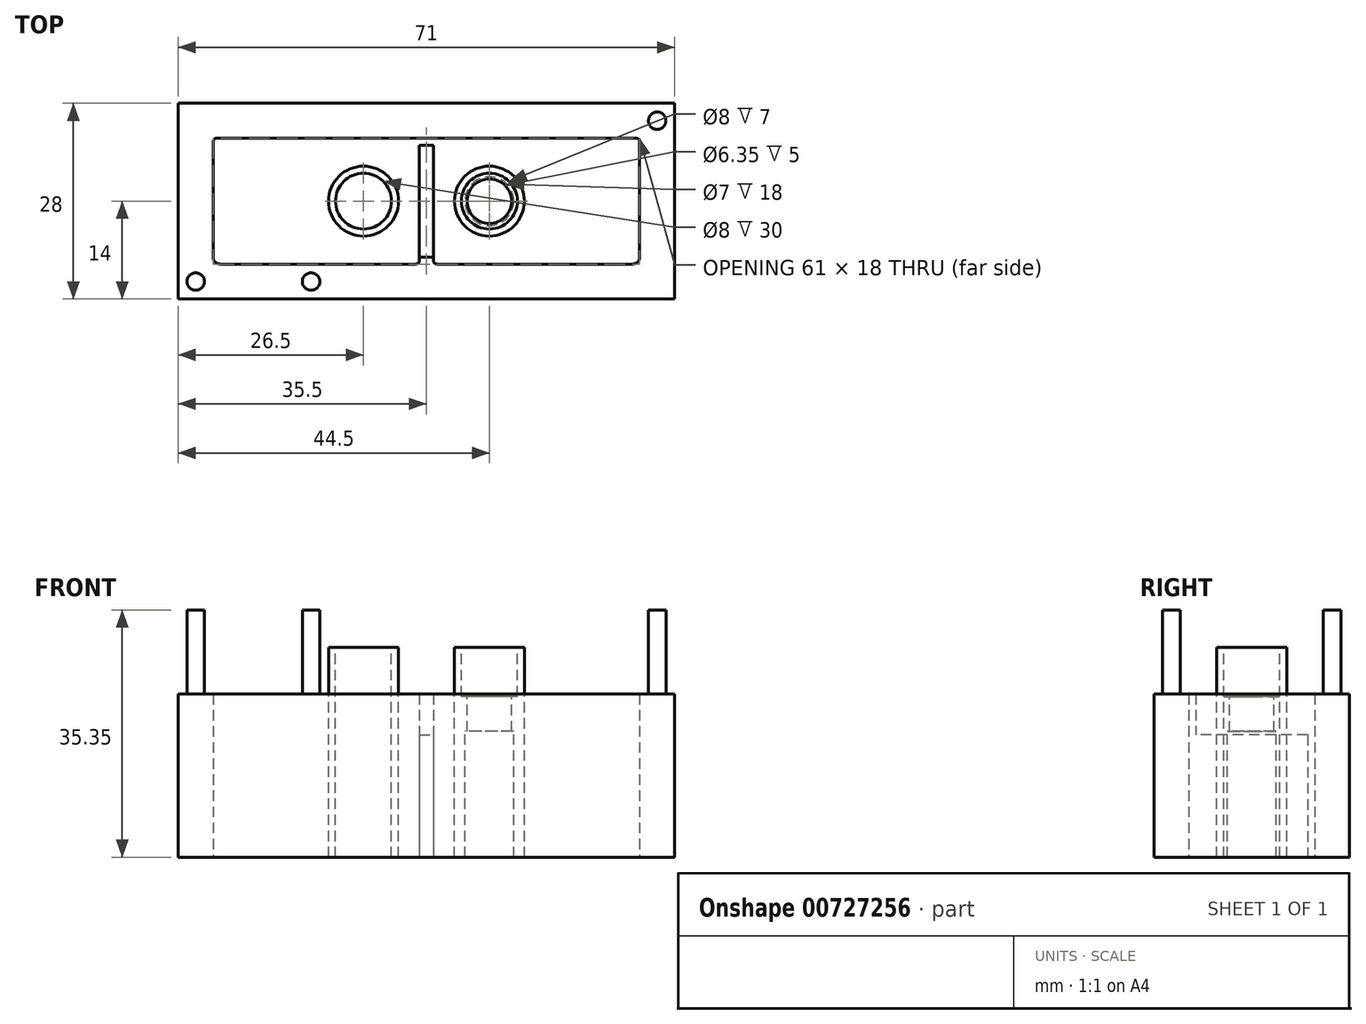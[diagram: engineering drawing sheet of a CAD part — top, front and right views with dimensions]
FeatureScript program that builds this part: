
annotation { "Feature Type Name" : "Feature", "Feature Type Description" : "" }
export const myFeature = defineFeature(function(context is Context, id is Id, definition is map)
    precondition{}
    {
        {
            var Q0;
            Q0=qCreatedBy(makeId("Top.planeOp"),FACE);
            var sketch = newSketch(context, id + "F0", { "sketchPlane" : qUnion([Q0])});
            skLineSegment(sketch, "E0.bottom", {"start": v(-35.5, -14) * mm, "end": v(35.5, -14) * mm});
            skLineSegment(sketch, "E0.top", {"start": v(-35.5, 14) * mm, "end": v(35.5, 14) * mm});
            skLineSegment(sketch, "E0.left", {"start": v(-35.5, -14) * mm, "end": v(-35.5, 14) * mm});
            skLineSegment(sketch, "E0.right", {"start": v(35.5, -14) * mm, "end": v(35.5, 14) * mm});
            skPoint(sketch, "E0.middle", {"position": v(0, 0) * mm});
            skLineSegment(sketch, "E1.bottom", {"start": v(-30.5, -9) * mm, "end": v(30.5, -9) * mm});
            skLineSegment(sketch, "E1.top", {"start": v(-30.5, 9) * mm, "end": v(30.5, 9) * mm});
            skLineSegment(sketch, "E1.left", {"start": v(-30.5, -9) * mm, "end": v(-30.5, 9) * mm});
            skLineSegment(sketch, "E1.right", {"start": v(30.5, -9) * mm, "end": v(30.5, 9) * mm});
            skCircle(sketch, "E2", {"center": v(-9, 0) * mm, "radius": 5 * mm});
            skCircle(sketch, "E3", {"center": v(-20.4, 0) * mm, "radius": 5 * mm});
            skCircle(sketch, "E4", {"center": v(9, 0) * mm, "radius": 5 * mm});
            skCircle(sketch, "E5", {"center": v(20.4, 0) * mm, "radius": 5 * mm});
            skLineSegment(sketch, "E6.bottom", {"start": v(-1, 9) * mm, "end": v(1, 9) * mm});
            skLineSegment(sketch, "E6.top", {"start": v(-1, 8) * mm, "end": v(1, 8) * mm});
            skLineSegment(sketch, "E6.left", {"start": v(-1, 9) * mm, "end": v(-1, 8) * mm});
            skLineSegment(sketch, "E6.right", {"start": v(1, 9) * mm, "end": v(1, 8) * mm});
            skLineSegment(sketch, "E7.MirrorCS", {"start": v(-1, -8) * mm, "end": v(1, -8) * mm});
            skLineSegment(sketch, "E8.MirrorCS", {"start": v(-1, -9) * mm, "end": v(1, -9) * mm});
            skLineSegment(sketch, "E9.MirrorCS", {"start": v(1, -9) * mm, "end": v(1, -8) * mm});
            skLineSegment(sketch, "E10.MirrorCS", {"start": v(-1, -9) * mm, "end": v(-1, -8) * mm});
            skLineSegment(sketch, "E11.left", {"start": v(-1, 8) * mm, "end": v(-1, -8) * mm});
            skLineSegment(sketch, "E11.right", {"start": v(1, 8) * mm, "end": v(1, -8) * mm});
            skSolve(sketch);
        }
        {
            var Q0;
            Q0=makeQuery(id+"F0.imprint","IMPRINT",FACE,{"disambiguationData":[TD([[makeQuery(id+"F0.imprint","IMPRINT",EDGE,{"derivedFrom":sQuery(id+"F0.wireOp",EDGE,"E0.bottom")}),1.0]])]});
            var Q1;
            Q1 = qSketchRegion(id + "F0", true);
            var Q2;
            Q2=makeQuery(id+"F0.imprint","IMPRINT",FACE,{"disambiguationData":[TD([[makeQuery(id+"F0.imprint","IMPRINT",EDGE,{"derivedFrom":sQuery(id+"F0.wireOp",EDGE,"E1.bottom")}),1.0]])]});
            var Q3;
            Q3=makeQuery(id+"F0.imprint","IMPRINT",FACE,{"disambiguationData":[TD([[makeQuery(id+"F0.imprint","IMPRINT",EDGE,{"derivedFrom":sQuery(id+"F0.wireOp",EDGE,"E3")}),1.0]])]});
            var Q4;
            Q4=makeQuery(id+"F0.imprint","IMPRINT",FACE,{"disambiguationData":[TD([[makeQuery(id+"F0.imprint","IMPRINT",EDGE,{"derivedFrom":sQuery(id+"F0.wireOp",EDGE,"E2")}),1.0]])]});
            var Q5;
            Q5=makeQuery(id+"F0.imprint","IMPRINT",FACE,{"disambiguationData":[TD([[makeQuery(id+"F0.imprint","IMPRINT",EDGE,{"derivedFrom":sQuery(id+"F0.wireOp",EDGE,"E4")}),1.0]])]});
            var Q6;
            Q6=makeQuery(id+"F0.imprint","IMPRINT",FACE,{"disambiguationData":[TD([[makeQuery(id+"F0.imprint","IMPRINT",EDGE,{"derivedFrom":sQuery(id+"F0.wireOp",EDGE,"E5")}),1.0]])]});
            var Q7;
            Q7=makeQuery(id+"F0.imprint","IMPRINT",FACE,{"disambiguationData":[TD([[makeQuery(id+"F0.imprint","IMPRINT",EDGE,{"derivedFrom":sQuery(id+"F0.wireOp",EDGE,"E6.bottom")}),-1.0]])]});
            var Q8;
            Q8=makeQuery(id+"F0.imprint","IMPRINT",FACE,{"disambiguationData":[TD([[makeQuery(id+"F0.imprint","IMPRINT",EDGE,{"derivedFrom":sQuery(id+"F0.wireOp",EDGE,"E7.MirrorCS")}),-1.0]])]});
            var Q9;
            Q9=makeQuery(id+"F0.imprint","IMPRINT",FACE,{"disambiguationData":[TD([[makeQuery(id+"F0.imprint","IMPRINT",EDGE,{"derivedFrom":sQuery(id+"F0.wireOp",EDGE,"E6.top")}),-1.0]])]});
            var Q10;
            Q10=makeQuery(id+"F0.imprint","IMPRINT",FACE,{"disambiguationData":[TD([[makeQuery(id+"F0.imprint","IMPRINT",EDGE,{"derivedFrom":sQuery(id+"F0.wireOp",EDGE,"E8.MirrorCS")}),1.0]])]});
            extrude(context, id + "F1", {"entities" : qUnion([Q0, Q1, Q2, Q3, Q4, Q5, Q6, Q7, Q8, Q9, Q10]), "depth" : 5 * mm, "offsetDistance" : 25 * mm});
        }
        {
            var Q0;
            Q0=makeQuery(id+"F0.imprint","IMPRINT",FACE,{"disambiguationData":[TD([[makeQuery(id+"F0.imprint","IMPRINT",EDGE,{"derivedFrom":sQuery(id+"F0.wireOp",EDGE,"E0.bottom")}),1.0]])]});
            var Q1;
            Q1=makeQuery(id+"F0.imprint","IMPRINT",FACE,{"disambiguationData":[TD([[makeQuery(id+"F0.imprint","IMPRINT",EDGE,{"derivedFrom":sQuery(id+"F0.wireOp",EDGE,"E6.bottom")}),-1.0]])]});
            var Q2;
            Q2=makeQuery(id+"F0.imprint","IMPRINT",FACE,{"disambiguationData":[TD([[makeQuery(id+"F0.imprint","IMPRINT",EDGE,{"derivedFrom":sQuery(id+"F0.wireOp",EDGE,"E7.MirrorCS")}),-1.0]])]});
            var Q3;
            Q3=makeQuery(id+"F0.imprint","IMPRINT",FACE,{"disambiguationData":[TD([[makeQuery(id+"F0.imprint","IMPRINT",EDGE,{"derivedFrom":sQuery(id+"F0.wireOp",EDGE,"E8.MirrorCS")}),1.0]])]});
            extrude(context, id + "F2", {"entities" : qUnion([Q0, Q1, Q2, Q3]), "operationType" : NewBodyOperationType.ADD, "depth" : (5 + 25 - 1 + 6.35) * mm, "offsetDistance" : 25 * mm});
        }
        {
            var Q0;
            Q0=makeQuery(id+"F0.imprint","IMPRINT",FACE,{"disambiguationData":[TD([[makeQuery(id+"F0.imprint","IMPRINT",EDGE,{"derivedFrom":sQuery(id+"F0.wireOp",EDGE,"E6.top")}),-1.0]])]});
            extrude(context, id + "F3", {"entities" : qUnion([Q0]), "operationType" : NewBodyOperationType.ADD, "depth" : (5 + 12.5) * mm, "offsetDistance" : 25 * mm});
        }
        {
            var Q0;
            Q0=makeQuery(id+"F2.opExtrude","SWEPT_EDGE",EDGE,{"disambiguationData":[OSD([sQuery(id+"F0.wireOp",EDGE,"E1.top"),sQuery(id+"F0.wireOp",EDGE,"E6.bottom"),sQuery(id+"F0.wireOp",EDGE,"E6.left")])]});
            var Q1;
            Q1=makeQuery(id+"F2.opExtrude","SWEPT_EDGE",EDGE,{"disambiguationData":[OSD([sQuery(id+"F0.wireOp",EDGE,"E1.top"),sQuery(id+"F0.wireOp",EDGE,"E6.bottom"),sQuery(id+"F0.wireOp",EDGE,"E6.right")])]});
            var Q2;
            Q2=makeQuery(id+"F2.opExtrude","SWEPT_EDGE",EDGE,{"disambiguationData":[OSD([sQuery(id+"F0.wireOp",EDGE,"E1.bottom"),sQuery(id+"F0.wireOp",EDGE,"E8.MirrorCS"),sQuery(id+"F0.wireOp",EDGE,"E10.MirrorCS")])]});
            var Q3;
            Q3=makeQuery(id+"F2.opExtrude","SWEPT_EDGE",EDGE,{"disambiguationData":[OSD([sQuery(id+"F0.wireOp",EDGE,"E1.bottom"),sQuery(id+"F0.wireOp",EDGE,"E8.MirrorCS"),sQuery(id+"F0.wireOp",EDGE,"E9.MirrorCS")])]});
            fillet(context, id + "F4", {"entities" : qUnion([Q0, Q1, Q2, Q3]), "tangentPropagation" : true, "radius" : 0.5 * mm, "defaultsChanged" : true, "vertexSettings" : [], "allowEdgeOverflow" : false});
        }
        {
            var Q0;
            Q0=makeQuery(id+"F0.imprint","IMPRINT",FACE,{"disambiguationData":[TD([[makeQuery(id+"F0.imprint","IMPRINT",EDGE,{"derivedFrom":sQuery(id+"F0.wireOp",EDGE,"E3")}),1.0]])]});
            var Q1;
            Q1=makeQuery(id+"F0.imprint","IMPRINT",FACE,{"disambiguationData":[TD([[makeQuery(id+"F0.imprint","IMPRINT",EDGE,{"derivedFrom":sQuery(id+"F0.wireOp",EDGE,"E5")}),1.0]])]});
            var Q2;
            Q2=makeQuery(id+"F0.imprint","IMPRINT",FACE,{"disambiguationData":[TD([[makeQuery(id+"F0.imprint","IMPRINT",EDGE,{"derivedFrom":sQuery(id+"F0.wireOp",EDGE,"E2")}),1.0]])]});
            var Q3;
            Q3=makeQuery(id+"F0.imprint","IMPRINT",FACE,{"disambiguationData":[TD([[makeQuery(id+"F0.imprint","IMPRINT",EDGE,{"derivedFrom":sQuery(id+"F0.wireOp",EDGE,"E4")}),1.0]])]});
            extrude(context, id + "F5", {"entities" : qUnion([Q0, Q1, Q2, Q3]), "operationType" : NewBodyOperationType.REMOVE, "depth" : 5 * mm, "offsetDistance" : 25 * mm});
        }
        {
            var Q0;
            Q0=qCreatedBy(makeId("Front.planeOp"),FACE);
            var sketch = newSketch(context, id + "F6", { "sketchPlane" : qUnion([Q0])});
            skLineSegment(sketch, "E12.bottom", {"start": v(-14, 0) * mm, "end": v(-13, 0) * mm});
            skLineSegment(sketch, "E12.top", {"start": v(-14, 30) * mm, "end": v(-13, 30) * mm});
            skLineSegment(sketch, "E12.left", {"start": v(-14, 0) * mm, "end": v(-14, 30) * mm});
            skLineSegment(sketch, "E12.right", {"start": v(-13, 0) * mm, "end": v(-13, 30) * mm});
            skLineSegment(sketch, "E13.bottom", {"start": v(-13, 18) * mm, "end": v(-9, 18) * mm});
            skLineSegment(sketch, "E13.top", {"start": v(-13, 23) * mm, "end": v(-9, 23) * mm});
            skLineSegment(sketch, "E13.left", {"start": v(-13, 23) * mm, "end": v(-13, 18) * mm});
            skLineSegment(sketch, "E13.right", {"start": v(-9, 23) * mm, "end": v(-9, 18) * mm});
            skLineSegment(sketch, "E14.bottom", {"start": v(-13, 23) * mm, "end": v(-12.18, 23) * mm});
            skLineSegment(sketch, "E14.top", {"start": v(-13, 18) * mm, "end": v(-12.18, 18) * mm});
            skLineSegment(sketch, "E14.right", {"start": v(-12.18, 23) * mm, "end": v(-12.18, 18) * mm});
            skLineSegment(sketch, "E15.bottom", {"start": v(-13, 18) * mm, "end": v(-12.5, 18) * mm});
            skLineSegment(sketch, "E15.top", {"start": v(-13, 0) * mm, "end": v(-12.5, 0) * mm});
            skLineSegment(sketch, "E15.left", {"start": v(-13, 18) * mm, "end": v(-13, 0) * mm});
            skLineSegment(sketch, "E15.right", {"start": v(-12.5, 18) * mm, "end": v(-12.5, 0) * mm});
            skLineSegment(sketch, "E16.MirrorCS", {"start": v(13, 18) * mm, "end": v(12.5, 18) * mm});
            skLineSegment(sketch, "E17.MirrorCS", {"start": v(13, 0) * mm, "end": v(12.5, 0) * mm});
            skLineSegment(sketch, "E18.MirrorCS", {"start": v(13, 18) * mm, "end": v(12.18, 18) * mm});
            skLineSegment(sketch, "E19.MirrorCS", {"start": v(13, 23) * mm, "end": v(12.18, 23) * mm});
            skLineSegment(sketch, "E20.MirrorCS", {"start": v(14, 30) * mm, "end": v(13, 30) * mm});
            skLineSegment(sketch, "E21.MirrorCS", {"start": v(14, 0) * mm, "end": v(13, 0) * mm});
            skLineSegment(sketch, "E22.MirrorCS", {"start": v(13, 23) * mm, "end": v(13, 18) * mm});
            skLineSegment(sketch, "E23.MirrorCS", {"start": v(13, 18) * mm, "end": v(13, 0) * mm});
            skLineSegment(sketch, "E24.MirrorCS", {"start": v(14, 0) * mm, "end": v(14, 30) * mm});
            skLineSegment(sketch, "E25.MirrorCS", {"start": v(13, 0) * mm, "end": v(13, 30) * mm});
            skLineSegment(sketch, "E26.MirrorCS", {"start": v(12.18, 23) * mm, "end": v(12.18, 18) * mm});
            skLineSegment(sketch, "E27.MirrorCS", {"start": v(13, 18) * mm, "end": v(9, 18) * mm});
            skLineSegment(sketch, "E28.MirrorCS", {"start": v(12.5, 18) * mm, "end": v(12.5, 0) * mm});
            skLineSegment(sketch, "E29.MirrorCS", {"start": v(13, 23) * mm, "end": v(9, 23) * mm});
            skLineSegment(sketch, "E30.MirrorCS", {"start": v(9, 23) * mm, "end": v(9, 18) * mm});
            skSolve(sketch);
        }
        {
            var Q0;
            Q0=makeQuery(id+"F6.imprint","IMPRINT",FACE,{"disambiguationData":[TD([[makeQuery(id+"F6.imprint","IMPRINT",EDGE,{"derivedFrom":sQuery(id+"F6.wireOp",EDGE,"E12.bottom")}),1.0]])]});
            var Q1;
            Q1=makeQuery(id+"F6.imprint","IMPRINT",FACE,{"disambiguationData":[TD([[makeQuery(id+"F6.imprint","IMPRINT",EDGE,{"derivedFrom":sQuery(id+"F6.wireOp",EDGE,"E14.bottom")}),-1.0]])]});
            var Q2;
            Q2=makeQuery(id+"F6.imprint","IMPRINT",FACE,{"disambiguationData":[TD([[makeQuery(id+"F6.imprint","IMPRINT",EDGE,{"derivedFrom":sQuery(id+"F6.wireOp",EDGE,"E15.bottom")}),-1.0]])]});
            var Q3;
            Q3=sQuery(id+"F6.wireOp",EDGE,"E13.right");
            revolve(context, id + "F7", {"operationType" : NewBodyOperationType.ADD, "surfaceOperationType" : NewSurfaceOperationType.NEW, "entities" : qUnion([Q0, Q1, Q2]), "axis" : qUnion([Q3]), "revolveType" : RevolveType.FULL});
        }
        {
            var Q0;
            {var subQ2=sQuery(id+"F6.wireOp",EDGE,"E26.MirrorCS");Q0=makeQuery(id+"F6.imprint","IMPRINT",FACE,{"disambiguationData":[TD([[makeQuery(id+"F6.imprint","IMPRINT",EDGE,{"derivedFrom":subQ2}),1.0]])]});}
            var Q1;
            {var subQ3=sQuery(id+"F6.wireOp",EDGE,"E20.MirrorCS");Q1=makeQuery(id+"F6.imprint","IMPRINT",FACE,{"disambiguationData":[TD([[makeQuery(id+"F6.imprint","IMPRINT",EDGE,{"derivedFrom":subQ3}),1.0]])]});}
            var Q2;
            {var subQ0=sQuery(id+"F6.wireOp",EDGE,"E17.MirrorCS");Q2=makeQuery(id+"F6.imprint","IMPRINT",FACE,{"disambiguationData":[TD([[makeQuery(id+"F6.imprint","IMPRINT",EDGE,{"derivedFrom":subQ0}),-1.0]])]});}
            var Q3;
            Q3=sQuery(id+"F6.wireOp",EDGE,"E30.MirrorCS");
            revolve(context, id + "F8", {"operationType" : NewBodyOperationType.ADD, "surfaceOperationType" : NewSurfaceOperationType.NEW, "entities" : qUnion([Q0, Q1, Q2]), "axis" : qUnion([Q3]), "revolveType" : RevolveType.FULL});
        }
        {
            var Q0;
            {var subQ0=sQuery(id+"F0.wireOp",EDGE,"E0.left");Q0=makeQuery(id+"F2.boolean.opBoolean","MERGE",FACE,{"derivedFrom":[makeQuery(id+"F1.opExtrude","SWEPT_FACE",FACE,{"disambiguationData":[OSD([subQ0])]}),makeQuery(id+"F2.opExtrude","SWEPT_FACE",FACE,{"disambiguationData":[OSD([subQ0])]})]});}
            var sketch = newSketch(context, id + "F9", { "sketchPlane" : qUnion([Q0])});
            skCircle(sketch, "E31", {"center": v(0, 29) * mm, "radius": 3.25 * mm});
            skCircle(sketch, "E32", {"center": v(-4.3, 33.3) * mm, "radius": 1.25 * mm});
            skLineSegment(sketch, "E33", {"start": v(-13.65, 29) * mm, "end": v(14.35, 29) * mm});
            skLineSegment(sketch, "E34", {"start": v(0, 35.35) * mm, "end": v(0, 21.85) * mm});
            skCircle(sketch, "E35.MirrorC", {"center": v(-4.3, 24.7) * mm, "radius": 1.25 * mm});
            skCircle(sketch, "E36.MirrorC", {"center": v(4.3, 33.3) * mm, "radius": 1.25 * mm});
            skCircle(sketch, "E37.MirrorC", {"center": v(4.3, 24.7) * mm, "radius": 1.25 * mm});
            skSolve(sketch);
        }
        {
            var Q0;
            Q0=makeQuery(id+"F2.opExtrude","CAP_FACE",FACE,{"disambiguationData":[OSD([sQuery(id+"F0.wireOp",EDGE,"E0.bottom"),sQuery(id+"F0.wireOp",EDGE,"E0.top"),sQuery(id+"F0.wireOp",EDGE,"E0.left"),sQuery(id+"F0.wireOp",EDGE,"E0.right"),sQuery(id+"F0.wireOp",EDGE,"E1.bottom"),sQuery(id+"F0.wireOp",EDGE,"E1.top"),sQuery(id+"F0.wireOp",EDGE,"E1.left"),sQuery(id+"F0.wireOp",EDGE,"E1.right")])],"isStart":false});
            var sketch = newSketch(context, id + "F10", { "sketchPlane" : qUnion([Q0])});
            skLineSegment(sketch, "E38.bottom", {"start": v(-35.5, 14) * mm, "end": v(35.5, 14) * mm});
            skLineSegment(sketch, "E38.top", {"start": v(-35.5, -14) * mm, "end": v(35.5, -14) * mm});
            skLineSegment(sketch, "E38.left", {"start": v(-35.5, 14) * mm, "end": v(-35.5, -14) * mm});
            skLineSegment(sketch, "E38.right", {"start": v(35.5, 14) * mm, "end": v(35.5, -14) * mm});
            skCircle(sketch, "E39", {"center": v(-33, 11.5) * mm, "radius": 1.25 * mm});
            skCircle(sketch, "E40.MirrorC", {"center": v(33, 11.5) * mm, "radius": 1.25 * mm});
            skCircle(sketch, "E41.MirrorC", {"center": v(-33, -11.5) * mm, "radius": 1.25 * mm});
            skCircle(sketch, "E42.MirrorC", {"center": v(33, -11.5) * mm, "radius": 1.25 * mm});
            skCircle(sketch, "E43", {"center": v(0, 11.5) * mm, "radius": 1.25 * mm});
            skPoint(sketch, "E43.centerSnap0", {"position": v(0, 14) * mm});
            skCircle(sketch, "E44", {"center": v(-16.5, 11.5) * mm, "radius": 1.25 * mm});
            skLineSegment(sketch, "E45", {"start": v(-33, 11.5) * mm, "end": v(33, 11.5) * mm});
            skLineSegment(sketch, "E46", {"start": v(-33, 11.5) * mm, "end": v(-33, -11.5) * mm});
            skLineSegment(sketch, "E47", {"start": v(-33, -11.5) * mm, "end": v(33, -11.5) * mm});
            skLineSegment(sketch, "E48", {"start": v(33, -11.5) * mm, "end": v(33, 11.5) * mm});
            skCircle(sketch, "E49.MirrorC", {"center": v(16.5, 11.5) * mm, "radius": 1.25 * mm});
            skCircle(sketch, "E50.MirrorC", {"center": v(-16.5, -11.5) * mm, "radius": 1.25 * mm});
            skCircle(sketch, "E51.MirrorC", {"center": v(0, -11.5) * mm, "radius": 1.25 * mm});
            skCircle(sketch, "E52.MirrorC", {"center": v(16.5, -11.5) * mm, "radius": 1.25 * mm});
            skSolve(sketch);
        }
        {
            var Q0;
            {var subQ0=sQuery(id+"F10.wireOp",EDGE,"E45");var subQ1=sQuery(id+"F10.wireOp",EDGE,"E39");var subQ2=makeQuery(id+"F10.imprint","INTERSECT",VERTEX,{"derivedFrom":[subQ1,subQ0]});Q0=makeQuery(id+"F10.imprint","IMPRINT",FACE,{"disambiguationData":[TD([[makeQuery(id+"F10.imprint","IMPRINT",EDGE,{"disambiguationData":[TD([[subQ2,1.0]])],"derivedFrom":subQ1}),1.0]])]});}
            var Q1;
            {var subQ0=sQuery(id+"F10.wireOp",EDGE,"E45");var subQ1=sQuery(id+"F10.wireOp",EDGE,"E39");var subQ2=makeQuery(id+"F10.imprint","INTERSECT",VERTEX,{"derivedFrom":[subQ1,subQ0]});Q1=makeQuery(id+"F10.imprint","IMPRINT",FACE,{"disambiguationData":[TD([[makeQuery(id+"F10.imprint","IMPRINT",EDGE,{"disambiguationData":[TD([[subQ2,-1.0]])],"derivedFrom":subQ1}),1.0]])]});}
            var Q2;
            {var subQ0=sQuery(id+"F10.wireOp",EDGE,"E45");var subQ1=sQuery(id+"F10.wireOp",EDGE,"E44");var subQ2=makeQuery(id+"F10.imprint","INTERSECT",VERTEX,{"disambiguationData":[OD(0.0)],"derivedFrom":[subQ1,subQ0]});Q2=makeQuery(id+"F10.imprint","IMPRINT",FACE,{"disambiguationData":[TD([[makeQuery(id+"F10.imprint","IMPRINT",EDGE,{"disambiguationData":[TD([[subQ2,-1.0]])],"derivedFrom":subQ1}),1.0]])]});}
            var Q3;
            {var subQ0=sQuery(id+"F10.wireOp",EDGE,"E45");var subQ1=sQuery(id+"F10.wireOp",EDGE,"E44");var subQ2=makeQuery(id+"F10.imprint","INTERSECT",VERTEX,{"disambiguationData":[OD(0.0)],"derivedFrom":[subQ1,subQ0]});Q3=makeQuery(id+"F10.imprint","IMPRINT",FACE,{"disambiguationData":[TD([[makeQuery(id+"F10.imprint","IMPRINT",EDGE,{"disambiguationData":[TD([[subQ2,1.0]])],"derivedFrom":subQ1}),1.0]])]});}
            var Q4;
            {var subQ0=sQuery(id+"F10.wireOp",EDGE,"E45");var subQ1=sQuery(id+"F10.wireOp",EDGE,"E43");var subQ2=makeQuery(id+"F10.imprint","INTERSECT",VERTEX,{"disambiguationData":[OD(0.0)],"derivedFrom":[subQ1,subQ0]});Q4=makeQuery(id+"F10.imprint","IMPRINT",FACE,{"disambiguationData":[TD([[makeQuery(id+"F10.imprint","IMPRINT",EDGE,{"disambiguationData":[TD([[subQ2,-1.0]])],"derivedFrom":subQ1}),1.0]])]});}
            var Q5;
            {var subQ0=sQuery(id+"F10.wireOp",EDGE,"E45");var subQ1=sQuery(id+"F10.wireOp",EDGE,"E43");var subQ2=makeQuery(id+"F10.imprint","INTERSECT",VERTEX,{"disambiguationData":[OD(0.0)],"derivedFrom":[subQ1,subQ0]});Q5=makeQuery(id+"F10.imprint","IMPRINT",FACE,{"disambiguationData":[TD([[makeQuery(id+"F10.imprint","IMPRINT",EDGE,{"disambiguationData":[TD([[subQ2,1.0]])],"derivedFrom":subQ1}),1.0]])]});}
            var Q6;
            {var subQ0=sQuery(id+"F10.wireOp",EDGE,"E49.MirrorC");var subQ1=sQuery(id+"F10.wireOp",EDGE,"E45");var subQ2=makeQuery(id+"F10.imprint","INTERSECT",VERTEX,{"disambiguationData":[OD(0.0)],"derivedFrom":[subQ1,subQ0]});Q6=makeQuery(id+"F10.imprint","IMPRINT",FACE,{"disambiguationData":[TD([[makeQuery(id+"F10.imprint","IMPRINT",EDGE,{"disambiguationData":[TD([[subQ2,-1.0]])],"derivedFrom":subQ1}),1.0]])]});}
            var Q7;
            {var subQ0=sQuery(id+"F10.wireOp",EDGE,"E49.MirrorC");var subQ1=sQuery(id+"F10.wireOp",EDGE,"E45");var subQ2=makeQuery(id+"F10.imprint","INTERSECT",VERTEX,{"disambiguationData":[OD(0.0)],"derivedFrom":[subQ1,subQ0]});Q7=makeQuery(id+"F10.imprint","IMPRINT",FACE,{"disambiguationData":[TD([[makeQuery(id+"F10.imprint","IMPRINT",EDGE,{"disambiguationData":[TD([[subQ2,-1.0]])],"derivedFrom":subQ1}),-1.0]])]});}
            var Q8;
            {var subQ0=sQuery(id+"F10.wireOp",EDGE,"E45");var subQ1=sQuery(id+"F10.wireOp",EDGE,"E40.MirrorC");var subQ2=makeQuery(id+"F10.imprint","INTERSECT",VERTEX,{"derivedFrom":[subQ1,subQ0]});Q8=makeQuery(id+"F10.imprint","IMPRINT",FACE,{"disambiguationData":[TD([[makeQuery(id+"F10.imprint","IMPRINT",EDGE,{"disambiguationData":[TD([[subQ2,1.0]])],"derivedFrom":subQ1}),-1.0]])]});}
            var Q9;
            {var subQ0=sQuery(id+"F10.wireOp",EDGE,"E45");var subQ1=sQuery(id+"F10.wireOp",EDGE,"E40.MirrorC");var subQ2=makeQuery(id+"F10.imprint","INTERSECT",VERTEX,{"derivedFrom":[subQ1,subQ0]});Q9=makeQuery(id+"F10.imprint","IMPRINT",FACE,{"disambiguationData":[TD([[makeQuery(id+"F10.imprint","IMPRINT",EDGE,{"disambiguationData":[TD([[subQ2,-1.0]])],"derivedFrom":subQ1}),-1.0]])]});}
            var Q10;
            {var subQ0=sQuery(id+"F10.wireOp",EDGE,"E46");var subQ1=sQuery(id+"F10.wireOp",EDGE,"E41.MirrorC");var subQ2=makeQuery(id+"F10.imprint","INTERSECT",VERTEX,{"derivedFrom":[subQ1,subQ0]});Q10=makeQuery(id+"F10.imprint","IMPRINT",FACE,{"disambiguationData":[TD([[makeQuery(id+"F10.imprint","IMPRINT",EDGE,{"disambiguationData":[TD([[subQ2,-1.0]])],"derivedFrom":subQ1}),-1.0]])]});}
            var Q11;
            {var subQ0=sQuery(id+"F10.wireOp",EDGE,"E46");var subQ1=sQuery(id+"F10.wireOp",EDGE,"E41.MirrorC");var subQ2=makeQuery(id+"F10.imprint","INTERSECT",VERTEX,{"derivedFrom":[subQ1,subQ0]});Q11=makeQuery(id+"F10.imprint","IMPRINT",FACE,{"disambiguationData":[TD([[makeQuery(id+"F10.imprint","IMPRINT",EDGE,{"disambiguationData":[TD([[subQ2,1.0]])],"derivedFrom":subQ1}),-1.0]])]});}
            var Q12;
            {var subQ0=sQuery(id+"F10.wireOp",EDGE,"E50.MirrorC");var subQ1=sQuery(id+"F10.wireOp",EDGE,"E47");var subQ2=makeQuery(id+"F10.imprint","INTERSECT",VERTEX,{"disambiguationData":[OD(0.0)],"derivedFrom":[subQ1,subQ0]});Q12=makeQuery(id+"F10.imprint","IMPRINT",FACE,{"disambiguationData":[TD([[makeQuery(id+"F10.imprint","IMPRINT",EDGE,{"disambiguationData":[TD([[subQ2,-1.0]])],"derivedFrom":subQ1}),1.0]])]});}
            var Q13;
            {var subQ0=sQuery(id+"F10.wireOp",EDGE,"E50.MirrorC");var subQ1=sQuery(id+"F10.wireOp",EDGE,"E47");var subQ2=makeQuery(id+"F10.imprint","INTERSECT",VERTEX,{"disambiguationData":[OD(0.0)],"derivedFrom":[subQ1,subQ0]});Q13=makeQuery(id+"F10.imprint","IMPRINT",FACE,{"disambiguationData":[TD([[makeQuery(id+"F10.imprint","IMPRINT",EDGE,{"disambiguationData":[TD([[subQ2,-1.0]])],"derivedFrom":subQ1}),-1.0]])]});}
            var Q14;
            {var subQ0=sQuery(id+"F10.wireOp",EDGE,"E51.MirrorC");var subQ1=sQuery(id+"F10.wireOp",EDGE,"E47");var subQ2=makeQuery(id+"F10.imprint","INTERSECT",VERTEX,{"disambiguationData":[OD(0.0)],"derivedFrom":[subQ1,subQ0]});Q14=makeQuery(id+"F10.imprint","IMPRINT",FACE,{"disambiguationData":[TD([[makeQuery(id+"F10.imprint","IMPRINT",EDGE,{"disambiguationData":[TD([[subQ2,-1.0]])],"derivedFrom":subQ1}),1.0]])]});}
            var Q15;
            {var subQ0=sQuery(id+"F10.wireOp",EDGE,"E51.MirrorC");var subQ1=sQuery(id+"F10.wireOp",EDGE,"E47");var subQ2=makeQuery(id+"F10.imprint","INTERSECT",VERTEX,{"disambiguationData":[OD(0.0)],"derivedFrom":[subQ1,subQ0]});Q15=makeQuery(id+"F10.imprint","IMPRINT",FACE,{"disambiguationData":[TD([[makeQuery(id+"F10.imprint","IMPRINT",EDGE,{"disambiguationData":[TD([[subQ2,-1.0]])],"derivedFrom":subQ1}),-1.0]])]});}
            var Q16;
            {var subQ0=sQuery(id+"F10.wireOp",EDGE,"E52.MirrorC");var subQ1=sQuery(id+"F10.wireOp",EDGE,"E47");var subQ2=makeQuery(id+"F10.imprint","INTERSECT",VERTEX,{"disambiguationData":[OD(0.0)],"derivedFrom":[subQ1,subQ0]});Q16=makeQuery(id+"F10.imprint","IMPRINT",FACE,{"disambiguationData":[TD([[makeQuery(id+"F10.imprint","IMPRINT",EDGE,{"disambiguationData":[TD([[subQ2,-1.0]])],"derivedFrom":subQ1}),1.0]])]});}
            var Q17;
            {var subQ0=sQuery(id+"F10.wireOp",EDGE,"E52.MirrorC");var subQ1=sQuery(id+"F10.wireOp",EDGE,"E47");var subQ2=makeQuery(id+"F10.imprint","INTERSECT",VERTEX,{"disambiguationData":[OD(0.0)],"derivedFrom":[subQ1,subQ0]});Q17=makeQuery(id+"F10.imprint","IMPRINT",FACE,{"disambiguationData":[TD([[makeQuery(id+"F10.imprint","IMPRINT",EDGE,{"disambiguationData":[TD([[subQ2,-1.0]])],"derivedFrom":subQ1}),-1.0]])]});}
            var Q18;
            {var subQ0=sQuery(id+"F10.wireOp",EDGE,"E47");var subQ1=sQuery(id+"F10.wireOp",EDGE,"E42.MirrorC");var subQ2=makeQuery(id+"F10.imprint","INTERSECT",VERTEX,{"derivedFrom":[subQ1,subQ0]});Q18=makeQuery(id+"F10.imprint","IMPRINT",FACE,{"disambiguationData":[TD([[makeQuery(id+"F10.imprint","IMPRINT",EDGE,{"disambiguationData":[TD([[subQ2,1.0]])],"derivedFrom":subQ1}),1.0]])]});}
            var Q19;
            {var subQ0=sQuery(id+"F10.wireOp",EDGE,"E47");var subQ1=sQuery(id+"F10.wireOp",EDGE,"E42.MirrorC");var subQ2=makeQuery(id+"F10.imprint","INTERSECT",VERTEX,{"derivedFrom":[subQ1,subQ0]});Q19=makeQuery(id+"F10.imprint","IMPRINT",FACE,{"disambiguationData":[TD([[makeQuery(id+"F10.imprint","IMPRINT",EDGE,{"disambiguationData":[TD([[subQ2,-1.0]])],"derivedFrom":subQ1}),1.0]])]});}
            extrude(context, id + "F11", {"entities" : qUnion([Q0, Q1, Q2, Q3, Q4, Q5, Q6, Q7, Q8, Q9, Q10, Q11, Q12, Q13, Q14, Q15, Q16, Q17, Q18, Q19]), "operationType" : NewBodyOperationType.REMOVE, "oppositeDirection" : true, "depth" : 12 * mm, "offsetDistance" : 25 * mm});
        }
        {
            var Q0;
            Q0=makeQuery(id+"F2.opExtrude","SWEPT_EDGE",EDGE,{"disambiguationData":[OSD([sQuery(id+"F0.wireOp",EDGE,"E1.bottom"),sQuery(id+"F0.wireOp",EDGE,"E1.left")])]});
            var Q1;
            Q1=makeQuery(id+"F2.opExtrude","SWEPT_EDGE",EDGE,{"disambiguationData":[OSD([sQuery(id+"F0.wireOp",EDGE,"E1.top"),sQuery(id+"F0.wireOp",EDGE,"E1.left")])]});
            var Q2;
            Q2=makeQuery(id+"F2.opExtrude","SWEPT_EDGE",EDGE,{"disambiguationData":[OSD([sQuery(id+"F0.wireOp",EDGE,"E1.top"),sQuery(id+"F0.wireOp",EDGE,"E1.right")])]});
            var Q3;
            Q3=makeQuery(id+"F2.opExtrude","SWEPT_EDGE",EDGE,{"disambiguationData":[OSD([sQuery(id+"F0.wireOp",EDGE,"E1.bottom"),sQuery(id+"F0.wireOp",EDGE,"E1.right")])]});
            fillet(context, id + "F12", {"entities" : qUnion([Q0, Q1, Q2, Q3]), "radius" : 1 * mm, "tangentPropagation" : true, "allowEdgeOverflow" : false});
        }
        {
            var Q0;
            {var subQ0=sQuery(id+"F0.wireOp",EDGE,"E0.right");Q0=makeQuery(id+"F2.boolean.opBoolean","MERGE",FACE,{"derivedFrom":[makeQuery(id+"F1.opExtrude","SWEPT_FACE",FACE,{"disambiguationData":[OSD([subQ0])]}),makeQuery(id+"F2.opExtrude","SWEPT_FACE",FACE,{"disambiguationData":[OSD([subQ0])]})]});}
            var sketch = newSketch(context, id + "F13", { "sketchPlane" : qUnion([Q0])});
            skCircle(sketch, "E53", {"center": v(0, 29) * mm, "radius": 3.25 * mm});
            skCircle(sketch, "E54", {"center": v(-4.3, 33.3) * mm, "radius": 1.25 * mm});
            skLineSegment(sketch, "E55", {"start": v(-14, 29) * mm, "end": v(14, 29) * mm});
            skCircle(sketch, "E56.MirrorC", {"center": v(-4.3, 24.7) * mm, "radius": 1.25 * mm});
            skCircle(sketch, "E57.MirrorC", {"center": v(4.3, 33.3) * mm, "radius": 1.25 * mm});
            skCircle(sketch, "E58.MirrorC", {"center": v(4.3, 24.7) * mm, "radius": 1.25 * mm});
            skSolve(sketch);
        }
        {
            var Q0;
            Q0 = qSketchRegion(id + "F9", true);
            extrude(context, id + "F14", {"entities" : qUnion([Q0]), "operationType" : NewBodyOperationType.REMOVE, "oppositeDirection" : true, "depth" : 5 * mm, "offsetDistance" : 25 * mm});
        }
        {
            var Q0;
            Q0 = qSketchRegion(id + "F13", true);
            extrude(context, id + "F15", {"entities" : qUnion([Q0]), "operationType" : NewBodyOperationType.REMOVE, "oppositeDirection" : true, "depth" : 5 * mm, "offsetDistance" : 25 * mm});
        }
    });
